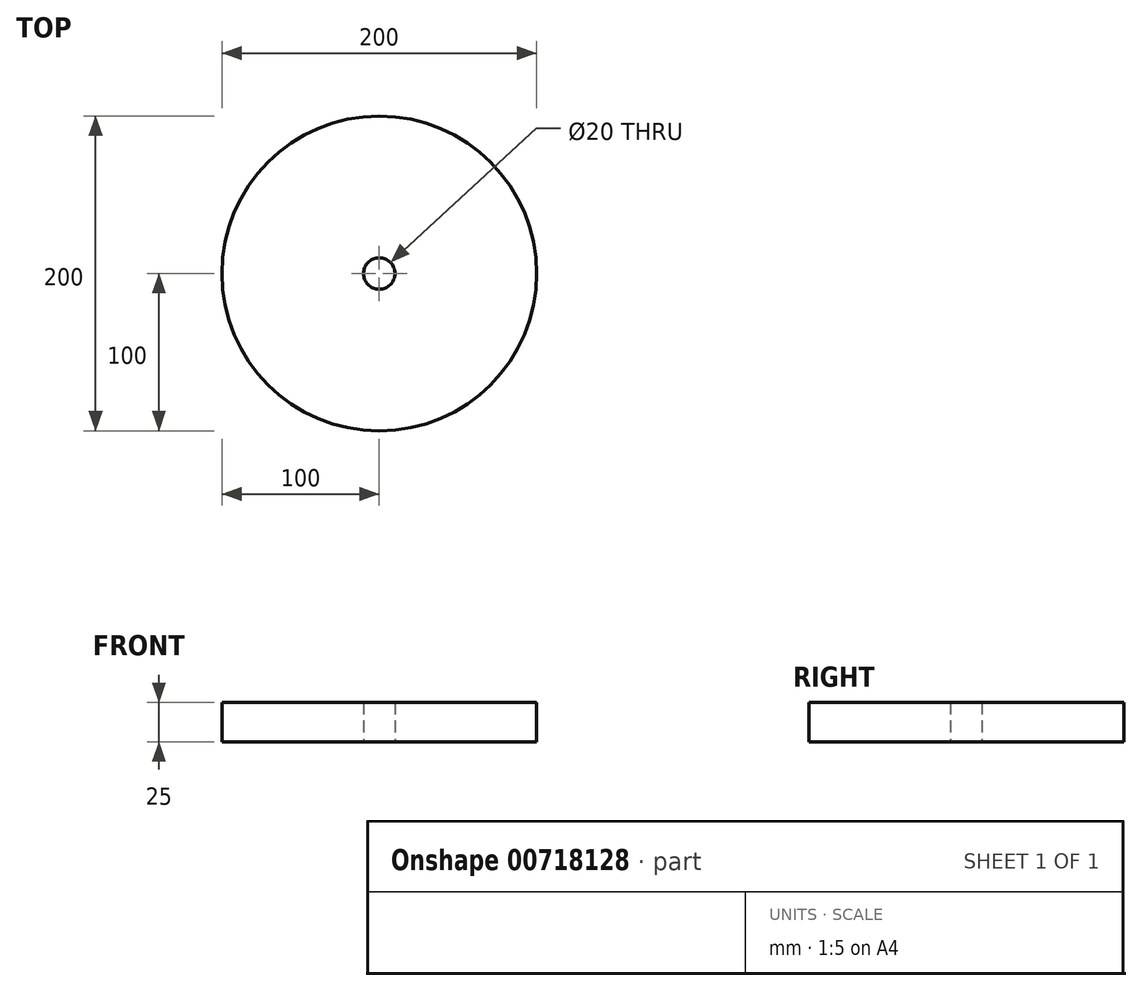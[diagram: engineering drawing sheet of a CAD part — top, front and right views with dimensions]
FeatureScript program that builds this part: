
annotation { "Feature Type Name" : "Feature", "Feature Type Description" : "" }
export const myFeature = defineFeature(function(context is Context, id is Id, definition is map)
    precondition{}
    {
        {
            var Q0;
            Q0=qCreatedBy(makeId("Top.planeOp"),FACE);
            var sketch = newSketch(context, id + "F0", { "sketchPlane" : qUnion([Q0])});
            skCircle(sketch, "E0", {"center": v(0, 0) * mm, "radius": 10 * mm});
            skCircle(sketch, "E1", {"center": v(0, 0) * mm, "radius": 100 * mm});
            skSolve(sketch);
        }
        {
            var Q0;
            Q0 = qSketchRegion(id + "F0", true);
            extrude(context, id + "F1", {"entities" : qUnion([Q0]), "depth" : 25 * mm, "offsetDistance" : 25 * mm});
        }
    });
